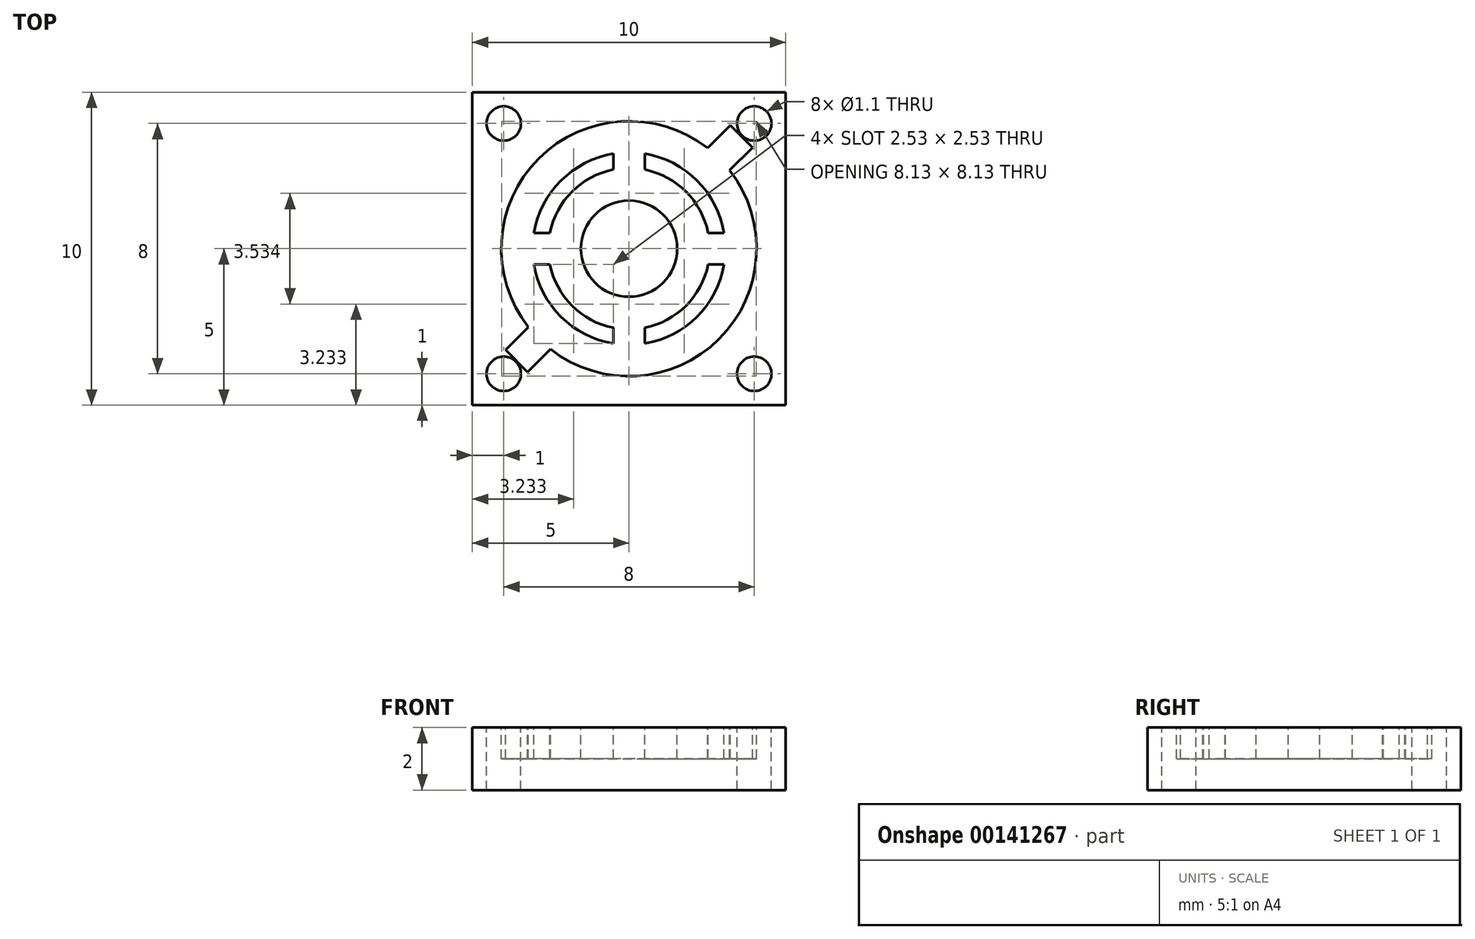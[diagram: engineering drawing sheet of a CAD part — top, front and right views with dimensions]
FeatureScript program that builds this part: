
annotation { "Feature Type Name" : "Feature", "Feature Type Description" : "" }
export const myFeature = defineFeature(function(context is Context, id is Id, definition is map)
    precondition{}
    {
        {
            var Q0;
            Q0=qCreatedBy(makeId("Top.planeOp"),FACE);
            var sketch = newSketch(context, id + "F0", { "sketchPlane" : qUnion([Q0])});
            skLineSegment(sketch, "E0.bottom", {"start": v(5, 5) * mm, "end": v(-5, 5) * mm});
            skLineSegment(sketch, "E0.top", {"start": v(5, -5) * mm, "end": v(-5, -5) * mm});
            skLineSegment(sketch, "E0.left", {"start": v(5, 5) * mm, "end": v(5, -5) * mm});
            skLineSegment(sketch, "E0.right", {"start": v(-5, 5) * mm, "end": v(-5, -5) * mm});
            skCircle(sketch, "E1", {"center": v(0, 0) * mm, "radius": 1.54 * mm});
            skArc(sketch, "E2", {"start": v(-2.53, -0.5) * mm, "mid": v(-1.82, -1.82) * mm, "end": v(-0.5, -2.53) * mm});
            skArc(sketch, "E3", {"start": v(-3.03, -0.5) * mm, "mid": v(-2.17, -2.17) * mm, "end": v(-0.5, -3.03) * mm});
            skArc(sketch, "E4", {"start": v(2.5, 3.21) * mm, "mid": v(-2.88, 2.88) * mm, "end": v(-3.21, -2.5) * mm});
            skLineSegment(sketch, "E5.trimOffspring", {"start": v(-2.53, 0.5) * mm, "end": v(-3.03, 0.5) * mm});
            skLineSegment(sketch, "E6.trimOffspring", {"start": v(-2.53, -0.5) * mm, "end": v(-3.03, -0.5) * mm});
            skLineSegment(sketch, "E7", {"start": v(2.53, -0.5) * mm, "end": v(3.03, -0.5) * mm});
            skLineSegment(sketch, "E8", {"start": v(2.53, 0.5) * mm, "end": v(3.03, 0.5) * mm});
            skArc(sketch, "E9.trimOffspring", {"start": v(2.53, 0.5) * mm, "mid": v(1.82, 1.82) * mm, "end": v(0.5, 2.53) * mm});
            skArc(sketch, "E10.trimOffspring", {"start": v(3.03, 0.5) * mm, "mid": v(2.17, 2.17) * mm, "end": v(0.5, 3.03) * mm});
            skArc(sketch, "E11.trimOffspring", {"start": v(0.5, -2.53) * mm, "mid": v(1.82, -1.82) * mm, "end": v(2.53, -0.5) * mm});
            skArc(sketch, "E12.trimOffspring", {"start": v(0.5, -3.03) * mm, "mid": v(2.17, -2.17) * mm, "end": v(3.03, -0.5) * mm});
            skLineSegment(sketch, "E13.trimOffspring", {"start": v(-0.5, -2.53) * mm, "end": v(-0.5, -3.03) * mm});
            skLineSegment(sketch, "E14.trimOffspring", {"start": v(0.5, -2.53) * mm, "end": v(0.5, -3.03) * mm});
            skArc(sketch, "E15.trimOffspring", {"start": v(-0.5, 2.53) * mm, "mid": v(-1.82, 1.82) * mm, "end": v(-2.53, 0.5) * mm});
            skArc(sketch, "E16.trimOffspring", {"start": v(-0.5, 3.03) * mm, "mid": v(-2.17, 2.17) * mm, "end": v(-3.03, 0.5) * mm});
            skLineSegment(sketch, "E17.trimOffspring", {"start": v(0.5, 2.53) * mm, "end": v(0.5, 3.03) * mm});
            skLineSegment(sketch, "E18.trimOffspring", {"start": v(-0.5, 2.53) * mm, "end": v(-0.5, 3.03) * mm});
            skLineSegment(sketch, "E19", {"start": v(3.6, 3.57) * mm, "end": v(3.24, 3.94) * mm});
            skLineSegment(sketch, "E20", {"start": v(3.6, 3.57) * mm, "end": v(3.94, 3.24) * mm});
            skLineSegment(sketch, "E21.MirrorCS", {"start": v(-3.57, -3.6) * mm, "end": v(-3.94, -3.24) * mm});
            skLineSegment(sketch, "E22.MirrorCS", {"start": v(-3.57, -3.6) * mm, "end": v(-3.24, -3.94) * mm});
            skLineSegment(sketch, "E23", {"start": v(-3.94, -3.24) * mm, "end": v(-3.21, -2.5) * mm});
            skLineSegment(sketch, "E24", {"start": v(-3.24, -3.94) * mm, "end": v(-2.5, -3.21) * mm});
            skArc(sketch, "E25.trimOffspring", {"start": v(-2.5, -3.21) * mm, "mid": v(2.88, -2.88) * mm, "end": v(3.21, 2.5) * mm});
            skLineSegment(sketch, "E26", {"start": v(3.94, 3.24) * mm, "end": v(3.21, 2.5) * mm});
            skLineSegment(sketch, "E27", {"start": v(3.24, 3.94) * mm, "end": v(2.5, 3.21) * mm});
            skCircle(sketch, "E28", {"center": v(-4, -4) * mm, "radius": 0.55 * mm});
            skLineSegment(sketch, "E29", {"start": v(-5, 0) * mm, "end": v(5, 0) * mm, "construction": true});
            skLineSegment(sketch, "E30", {"start": v(0, 5) * mm, "end": v(0, -5) * mm, "construction": true});
            skPoint(sketch, "E30.endSnap0", {"position": v(0, 5) * mm});
            skCircle(sketch, "E31.MirrorC", {"center": v(4, -4) * mm, "radius": 0.55 * mm});
            skCircle(sketch, "E32.MirrorC", {"center": v(-4, 4) * mm, "radius": 0.55 * mm});
            skCircle(sketch, "E33.MirrorC", {"center": v(4, 4) * mm, "radius": 0.55 * mm});
            skSolve(sketch);
        }
        {
            var Q0;
            Q0=makeQuery(id+"F0.imprint","IMPRINT",FACE,{"disambiguationData":[TD([[makeQuery(id+"F0.imprint","IMPRINT",EDGE,{"derivedFrom":sQuery(id+"F0.wireOp",EDGE,"E0.bottom")}),1.0]])]});
            var Q1;
            Q1=makeQuery(id+"F0.imprint","IMPRINT",FACE,{"disambiguationData":[TD([[makeQuery(id+"F0.imprint","IMPRINT",EDGE,{"derivedFrom":sQuery(id+"F0.wireOp",EDGE,"E1")}),-1.0]])]});
            var Q2;
            Q2=makeQuery(id+"F0.imprint","IMPRINT",FACE,{"disambiguationData":[TD([[makeQuery(id+"F0.imprint","IMPRINT",EDGE,{"derivedFrom":sQuery(id+"F0.wireOp",EDGE,"E2")}),-1.0]])]});
            var Q3;
            Q3=makeQuery(id+"F0.imprint","IMPRINT",FACE,{"disambiguationData":[TD([[makeQuery(id+"F0.imprint","IMPRINT",EDGE,{"derivedFrom":sQuery(id+"F0.wireOp",EDGE,"E5.trimOffspring")}),-1.0]])]});
            var Q4;
            Q4=makeQuery(id+"F0.imprint","IMPRINT",FACE,{"disambiguationData":[TD([[makeQuery(id+"F0.imprint","IMPRINT",EDGE,{"derivedFrom":sQuery(id+"F0.wireOp",EDGE,"E8")}),1.0]])]});
            var Q5;
            Q5=makeQuery(id+"F0.imprint","IMPRINT",FACE,{"disambiguationData":[TD([[makeQuery(id+"F0.imprint","IMPRINT",EDGE,{"derivedFrom":sQuery(id+"F0.wireOp",EDGE,"E7")}),-1.0]])]});
            var Q6;
            Q6=makeQuery(id+"F0.imprint","IMPRINT",FACE,{"disambiguationData":[TD([[makeQuery(id+"F0.imprint","IMPRINT",EDGE,{"derivedFrom":sQuery(id+"F0.wireOp",EDGE,"E1")}),1.0]])]});
            extrude(context, id + "F1", {"entities" : qUnion([Q0, Q1, Q2, Q3, Q4, Q5, Q6]), "oppositeDirection" : true, "depth" : 2 * mm});
        }
        {
            var Q0;
            Q0=makeQuery(id+"F0.imprint","IMPRINT",FACE,{"disambiguationData":[TD([[makeQuery(id+"F0.imprint","IMPRINT",EDGE,{"derivedFrom":sQuery(id+"F0.wireOp",EDGE,"E1")}),-1.0]])]});
            extrude(context, id + "F2", {"entities" : qUnion([Q0]), "operationType" : NewBodyOperationType.REMOVE, "oppositeDirection" : true, "depth" : 1 * mm});
        }
    });
